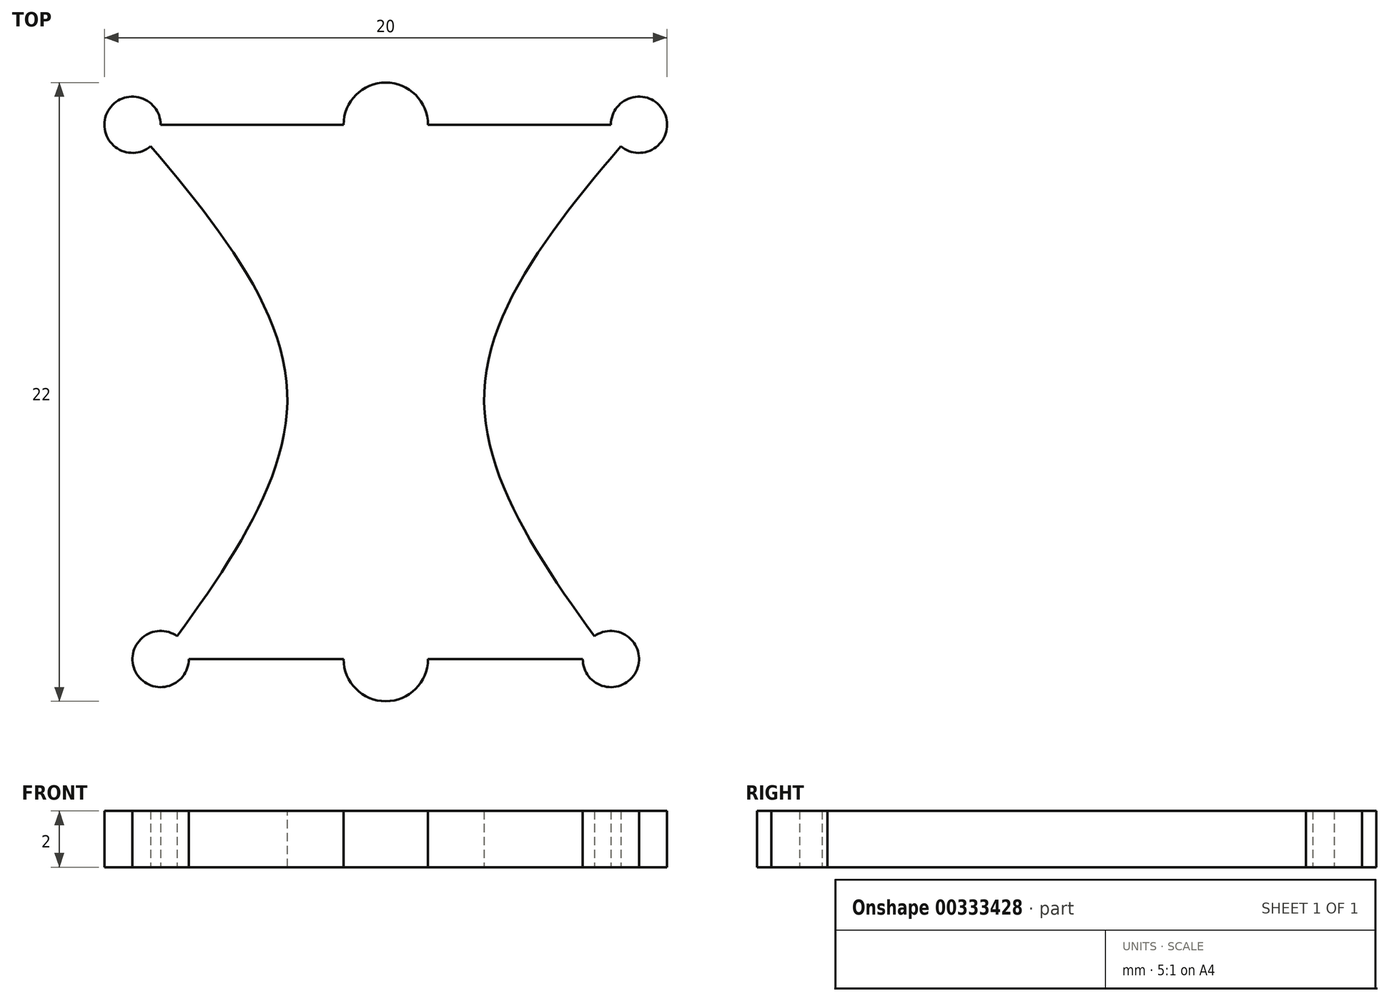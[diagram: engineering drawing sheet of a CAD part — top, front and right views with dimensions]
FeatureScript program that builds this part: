
annotation { "Feature Type Name" : "Feature", "Feature Type Description" : "" }
export const myFeature = defineFeature(function(context is Context, id is Id, definition is map)
    precondition{}
    {
        {
            var Q0;
            Q0=qCreatedBy(makeId("Top.planeOp"),FACE);
            var sketch = newSketch(context, id + "F0", { "sketchPlane" : qUnion([Q0])});
            skLineSegment(sketch, "E0", {"start": v(-9, 0) * mm, "end": v(9, 0) * mm});
            skCircle(sketch, "E1", {"center": v(0, 0) * mm, "radius": 1.5 * mm});
            skLineSegment(sketch, "E2", {"start": v(0, 0) * mm, "end": v(0, -19) * mm});
            skCircle(sketch, "E3", {"center": v(0, -19) * mm, "radius": 1.5 * mm});
            skLineSegment(sketch, "E4", {"start": v(-8, -19) * mm, "end": v(8, -19) * mm});
            skPoint(sketch, "E5", {"position": v(0, -9.5) * mm});
            skLineSegment(sketch, "E6", {"start": v(-3.5, -9.5) * mm, "end": v(3.5, -9.5) * mm});
            skFitSpline(sketch, "E7", {"points": [v(-8, -19) * mm, v(-3.5, -9.5) * mm, v(-9, 0) * mm], "startDerivative": vector(14.04, 19.3) * mm, "endDerivative": vector(-15.93, 18.7) * mm});
            skFitSpline(sketch, "E8", {"points": [v(8, -19) * mm, v(3.5, -9.5) * mm, v(9, 0) * mm], "startDerivative": vector(-14.04, 19.3) * mm, "endDerivative": vector(15.93, 18.7) * mm});
            skCircle(sketch, "E9", {"center": v(-9, 0) * mm, "radius": 1 * mm});
            skCircle(sketch, "E10", {"center": v(-8, -19) * mm, "radius": 1 * mm});
            skCircle(sketch, "E11.MirrorC", {"center": v(8, -19) * mm, "radius": 1 * mm});
            skCircle(sketch, "E12.MirrorC", {"center": v(9, 0) * mm, "radius": 1 * mm});
            skSolve(sketch);
        }
        {
            var Q0;
            {var subQ0=sQuery(id+"F0.wireOp",EDGE,"E7");var subQ1=sQuery(id+"F0.wireOp",EDGE,"E0");var subQ2=makeQuery(id+"F0.imprint","INTERSECT",VERTEX,{"derivedFrom":[subQ1,subQ0]});Q0=makeQuery(id+"F0.imprint","IMPRINT",FACE,{"disambiguationData":[TD([[makeQuery(id+"F0.imprint","IMPRINT",EDGE,{"disambiguationData":[TD([[subQ2,-1.0]])],"derivedFrom":subQ1}),1.0]])]});}
            var Q1;
            {var subQ0=sQuery(id+"F0.wireOp",EDGE,"E7");var subQ1=sQuery(id+"F0.wireOp",EDGE,"E0");var subQ2=makeQuery(id+"F0.imprint","INTERSECT",VERTEX,{"derivedFrom":[subQ1,subQ0]});Q1=makeQuery(id+"F0.imprint","IMPRINT",FACE,{"disambiguationData":[TD([[makeQuery(id+"F0.imprint","IMPRINT",EDGE,{"disambiguationData":[TD([[subQ2,-1.0]])],"derivedFrom":subQ1}),-1.0]])]});}
            var Q2;
            {var subQ7=sQuery(id+"F0.wireOp",EDGE,"E9");var subQ8=sQuery(id+"F0.wireOp",EDGE,"E0");var subQ9=makeQuery(id+"F0.imprint","INTERSECT",VERTEX,{"derivedFrom":[subQ8,subQ7]});Q2=makeQuery(id+"F0.imprint","IMPRINT",FACE,{"disambiguationData":[TD([[makeQuery(id+"F0.imprint","IMPRINT",EDGE,{"disambiguationData":[TD([[subQ9,-1.0]])],"derivedFrom":subQ8}),-1.0]])]});}
            var Q3;
            {var subQ0=sQuery(id+"F0.wireOp",EDGE,"E2");var subQ1=sQuery(id+"F0.wireOp",EDGE,"E0");var subQ2=makeQuery(id+"F0.imprint","INTERSECT",VERTEX,{"derivedFrom":[subQ1,subQ0]});Q3=makeQuery(id+"F0.imprint","IMPRINT",FACE,{"disambiguationData":[TD([[makeQuery(id+"F0.imprint","IMPRINT",EDGE,{"disambiguationData":[TD([[subQ2,1.0]])],"derivedFrom":subQ1}),-1.0]])]});}
            var Q4;
            {var subQ0=sQuery(id+"F0.wireOp",EDGE,"E0");var subQ1=makeQuery(id+"F0.imprint","INTERSECT",VERTEX,{"derivedFrom":[subQ0,sQuery(id+"F0.wireOp",EDGE,"E2")]});Q4=makeQuery(id+"F0.imprint","IMPRINT",FACE,{"disambiguationData":[TD([[makeQuery(id+"F0.imprint","IMPRINT",EDGE,{"disambiguationData":[TD([[subQ1,1.0]])],"derivedFrom":subQ0}),1.0]])]});}
            var Q5;
            {var subQ0=sQuery(id+"F0.wireOp",EDGE,"E2");var subQ1=sQuery(id+"F0.wireOp",EDGE,"E0");var subQ2=makeQuery(id+"F0.imprint","INTERSECT",VERTEX,{"derivedFrom":[subQ1,subQ0]});Q5=makeQuery(id+"F0.imprint","IMPRINT",FACE,{"disambiguationData":[TD([[makeQuery(id+"F0.imprint","IMPRINT",EDGE,{"disambiguationData":[TD([[subQ2,-1.0]])],"derivedFrom":subQ1}),-1.0]])]});}
            var Q6;
            {var subQ1=sQuery(id+"F0.wireOp",EDGE,"E1");var subQ7=sQuery(id+"F0.wireOp",EDGE,"E0");var subQ8=makeQuery(id+"F0.imprint","INTERSECT",VERTEX,{"disambiguationData":[OD(1.0)],"derivedFrom":[subQ7,subQ1]});Q6=makeQuery(id+"F0.imprint","IMPRINT",FACE,{"disambiguationData":[TD([[makeQuery(id+"F0.imprint","IMPRINT",EDGE,{"disambiguationData":[TD([[subQ8,-1.0]])],"derivedFrom":subQ7}),-1.0]])]});}
            var Q7;
            {var subQ0=sQuery(id+"F0.wireOp",EDGE,"E8");var subQ1=sQuery(id+"F0.wireOp",EDGE,"E0");var subQ2=makeQuery(id+"F0.imprint","INTERSECT",VERTEX,{"derivedFrom":[subQ1,subQ0]});Q7=makeQuery(id+"F0.imprint","IMPRINT",FACE,{"disambiguationData":[TD([[makeQuery(id+"F0.imprint","IMPRINT",EDGE,{"disambiguationData":[TD([[subQ2,1.0]])],"derivedFrom":subQ1}),-1.0]])]});}
            var Q8;
            {var subQ0=sQuery(id+"F0.wireOp",EDGE,"E8");var subQ1=sQuery(id+"F0.wireOp",EDGE,"E0");var subQ2=makeQuery(id+"F0.imprint","INTERSECT",VERTEX,{"derivedFrom":[subQ1,subQ0]});Q8=makeQuery(id+"F0.imprint","IMPRINT",FACE,{"disambiguationData":[TD([[makeQuery(id+"F0.imprint","IMPRINT",EDGE,{"disambiguationData":[TD([[subQ2,1.0]])],"derivedFrom":subQ1}),1.0]])]});}
            var Q9;
            {var subQ1=sQuery(id+"F0.wireOp",EDGE,"E6");var subQ3=sQuery(id+"F0.wireOp",EDGE,"E2");var subQ4=makeQuery(id+"F0.imprint","INTERSECT",VERTEX,{"derivedFrom":[subQ3,subQ1]});Q9=makeQuery(id+"F0.imprint","IMPRINT",FACE,{"disambiguationData":[TD([[makeQuery(id+"F0.imprint","IMPRINT",EDGE,{"disambiguationData":[TD([[subQ4,-1.0]])],"derivedFrom":subQ3}),-1.0]])]});}
            var Q10;
            {var subQ6=sQuery(id+"F0.wireOp",EDGE,"E6");var subQ8=sQuery(id+"F0.wireOp",EDGE,"E2");var subQ9=makeQuery(id+"F0.imprint","INTERSECT",VERTEX,{"derivedFrom":[subQ8,subQ6]});Q10=makeQuery(id+"F0.imprint","IMPRINT",FACE,{"disambiguationData":[TD([[makeQuery(id+"F0.imprint","IMPRINT",EDGE,{"disambiguationData":[TD([[subQ9,-1.0]])],"derivedFrom":subQ8}),1.0]])]});}
            var Q11;
            {var subQ0=sQuery(id+"F0.wireOp",EDGE,"E4");var subQ1=sQuery(id+"F0.wireOp",EDGE,"E2");var subQ2=makeQuery(id+"F0.imprint","INTERSECT",VERTEX,{"derivedFrom":[subQ1,subQ0]});Q11=makeQuery(id+"F0.imprint","IMPRINT",FACE,{"disambiguationData":[TD([[makeQuery(id+"F0.imprint","IMPRINT",EDGE,{"disambiguationData":[TD([[subQ2,1.0]])],"derivedFrom":subQ1}),-1.0]])]});}
            var Q12;
            {var subQ0=sQuery(id+"F0.wireOp",EDGE,"E4");var subQ1=sQuery(id+"F0.wireOp",EDGE,"E2");var subQ2=makeQuery(id+"F0.imprint","INTERSECT",VERTEX,{"derivedFrom":[subQ1,subQ0]});Q12=makeQuery(id+"F0.imprint","IMPRINT",FACE,{"disambiguationData":[TD([[makeQuery(id+"F0.imprint","IMPRINT",EDGE,{"disambiguationData":[TD([[subQ2,1.0]])],"derivedFrom":subQ1}),1.0]])]});}
            var Q13;
            {var subQ0=sQuery(id+"F0.wireOp",EDGE,"E4");var subQ1=sQuery(id+"F0.wireOp",EDGE,"E3");var subQ2=makeQuery(id+"F0.imprint","INTERSECT",VERTEX,{"disambiguationData":[OD(0.0)],"derivedFrom":[subQ1,subQ0]});Q13=makeQuery(id+"F0.imprint","IMPRINT",FACE,{"disambiguationData":[TD([[makeQuery(id+"F0.imprint","IMPRINT",EDGE,{"disambiguationData":[TD([[subQ2,1.0]])],"derivedFrom":subQ1}),1.0]])]});}
            var Q14;
            {var subQ0=sQuery(id+"F0.wireOp",EDGE,"E7");var subQ1=sQuery(id+"F0.wireOp",EDGE,"E4");var subQ2=makeQuery(id+"F0.imprint","INTERSECT",VERTEX,{"derivedFrom":[subQ1,subQ0]});Q14=makeQuery(id+"F0.imprint","IMPRINT",FACE,{"disambiguationData":[TD([[makeQuery(id+"F0.imprint","IMPRINT",EDGE,{"disambiguationData":[TD([[subQ2,-1.0]])],"derivedFrom":subQ1}),-1.0]])]});}
            var Q15;
            {var subQ0=sQuery(id+"F0.wireOp",EDGE,"E7");var subQ1=sQuery(id+"F0.wireOp",EDGE,"E4");var subQ2=makeQuery(id+"F0.imprint","INTERSECT",VERTEX,{"derivedFrom":[subQ1,subQ0]});Q15=makeQuery(id+"F0.imprint","IMPRINT",FACE,{"disambiguationData":[TD([[makeQuery(id+"F0.imprint","IMPRINT",EDGE,{"disambiguationData":[TD([[subQ2,-1.0]])],"derivedFrom":subQ1}),1.0]])]});}
            var Q16;
            {var subQ0=sQuery(id+"F0.wireOp",EDGE,"E8");var subQ1=sQuery(id+"F0.wireOp",EDGE,"E4");var subQ2=makeQuery(id+"F0.imprint","INTERSECT",VERTEX,{"derivedFrom":[subQ1,subQ0]});Q16=makeQuery(id+"F0.imprint","IMPRINT",FACE,{"disambiguationData":[TD([[makeQuery(id+"F0.imprint","IMPRINT",EDGE,{"disambiguationData":[TD([[subQ2,1.0]])],"derivedFrom":subQ1}),1.0]])]});}
            var Q17;
            {var subQ0=sQuery(id+"F0.wireOp",EDGE,"E8");var subQ1=sQuery(id+"F0.wireOp",EDGE,"E4");var subQ2=makeQuery(id+"F0.imprint","INTERSECT",VERTEX,{"derivedFrom":[subQ1,subQ0]});Q17=makeQuery(id+"F0.imprint","IMPRINT",FACE,{"disambiguationData":[TD([[makeQuery(id+"F0.imprint","IMPRINT",EDGE,{"disambiguationData":[TD([[subQ2,1.0]])],"derivedFrom":subQ1}),-1.0]])]});}
            extrude(context, id + "F1", {"entities" : qUnion([Q0, Q1, Q2, Q3, Q4, Q5, Q6, Q7, Q8, Q9, Q10, Q11, Q12, Q13, Q14, Q15, Q16, Q17]), "depth" : 2 * mm});
        }
    });
